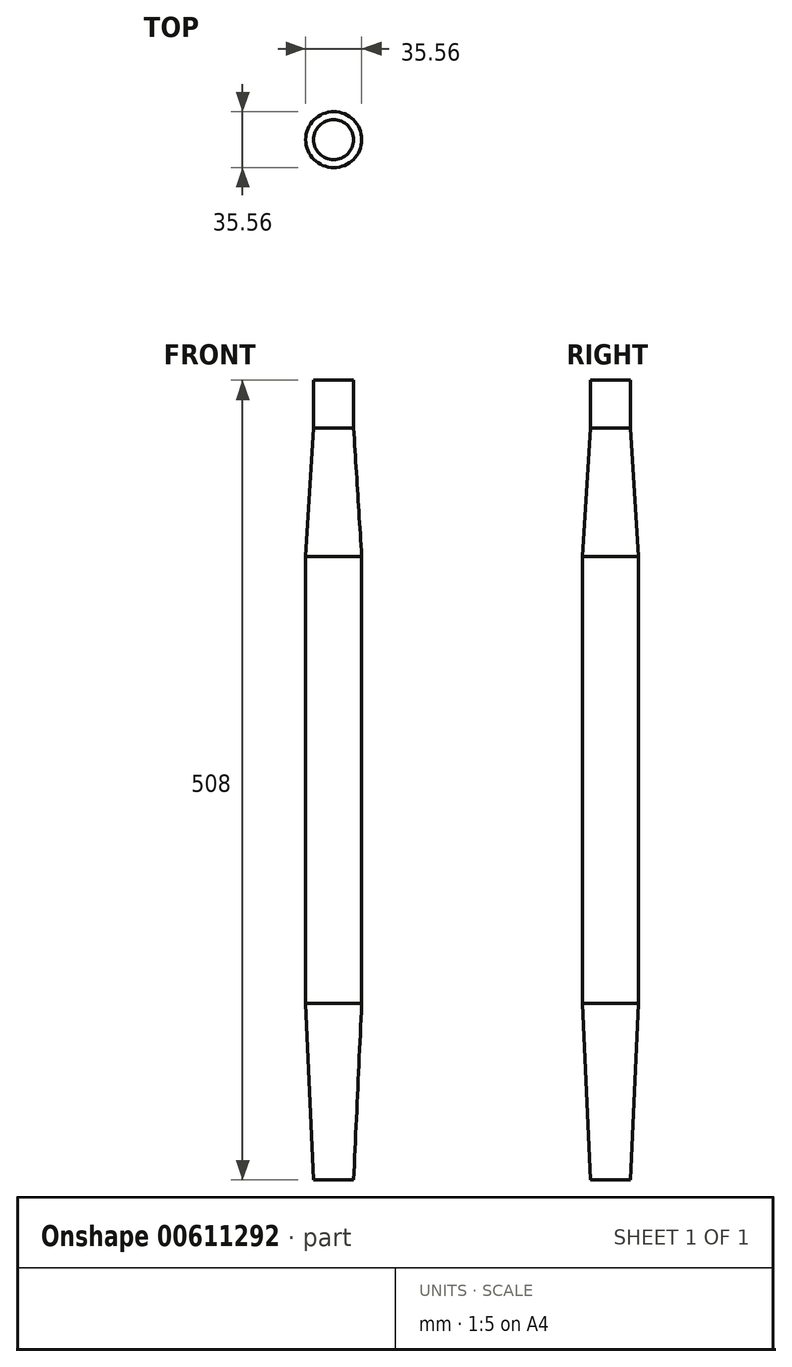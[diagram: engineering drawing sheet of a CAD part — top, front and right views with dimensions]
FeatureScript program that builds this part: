
annotation { "Feature Type Name" : "Feature", "Feature Type Description" : "" }
export const myFeature = defineFeature(function(context is Context, id is Id, definition is map)
    precondition{}
    {
        {
            var Q0;
            Q0=qCreatedBy(makeId("Front.planeOp"),FACE);
            var sketch = newSketch(context, id + "F0", { "sketchPlane" : qUnion([Q0])});
            skLineSegment(sketch, "E0", {"start": v(-20.75, 251.2) * mm, "end": v(-20.75, -256.8) * mm});
            skLineSegment(sketch, "E1", {"start": v(-20.75, 251.2) * mm, "end": v(-33.45, 251.2) * mm});
            skLineSegment(sketch, "E2", {"start": v(-38.53, 139.27) * mm, "end": v(-38.53, -144.82) * mm});
            skLineSegment(sketch, "E3", {"start": v(-38.53, -144.82) * mm, "end": v(-33.45, -256.8) * mm});
            skLineSegment(sketch, "E4", {"start": v(-33.45, -256.8) * mm, "end": v(-20.75, -256.8) * mm});
            skLineSegment(sketch, "E5", {"start": v(-33.45, 251.2) * mm, "end": v(-33.45, 220.71) * mm});
            skLineSegment(sketch, "E6", {"start": v(-33.45, 220.71) * mm, "end": v(-38.53, 139.27) * mm});
            skSolve(sketch);
        }
        {
            var Q0;
            Q0=makeQuery(id+"F0.imprint","IMPRINT",FACE,{"disambiguationData":[TD([[makeQuery(id+"F0.imprint","IMPRINT",EDGE,{"derivedFrom":sQuery(id+"F0.wireOp",EDGE,"E0")}),-1.0]])]});
            var Q1;
            Q1=sQuery(id+"F0.wireOp",EDGE,"E0");
            revolve(context, id + "F1", {"entities" : qUnion([Q0]), "axis" : qUnion([Q1]), "revolveType" : RevolveType.FULL});
        }
    });
